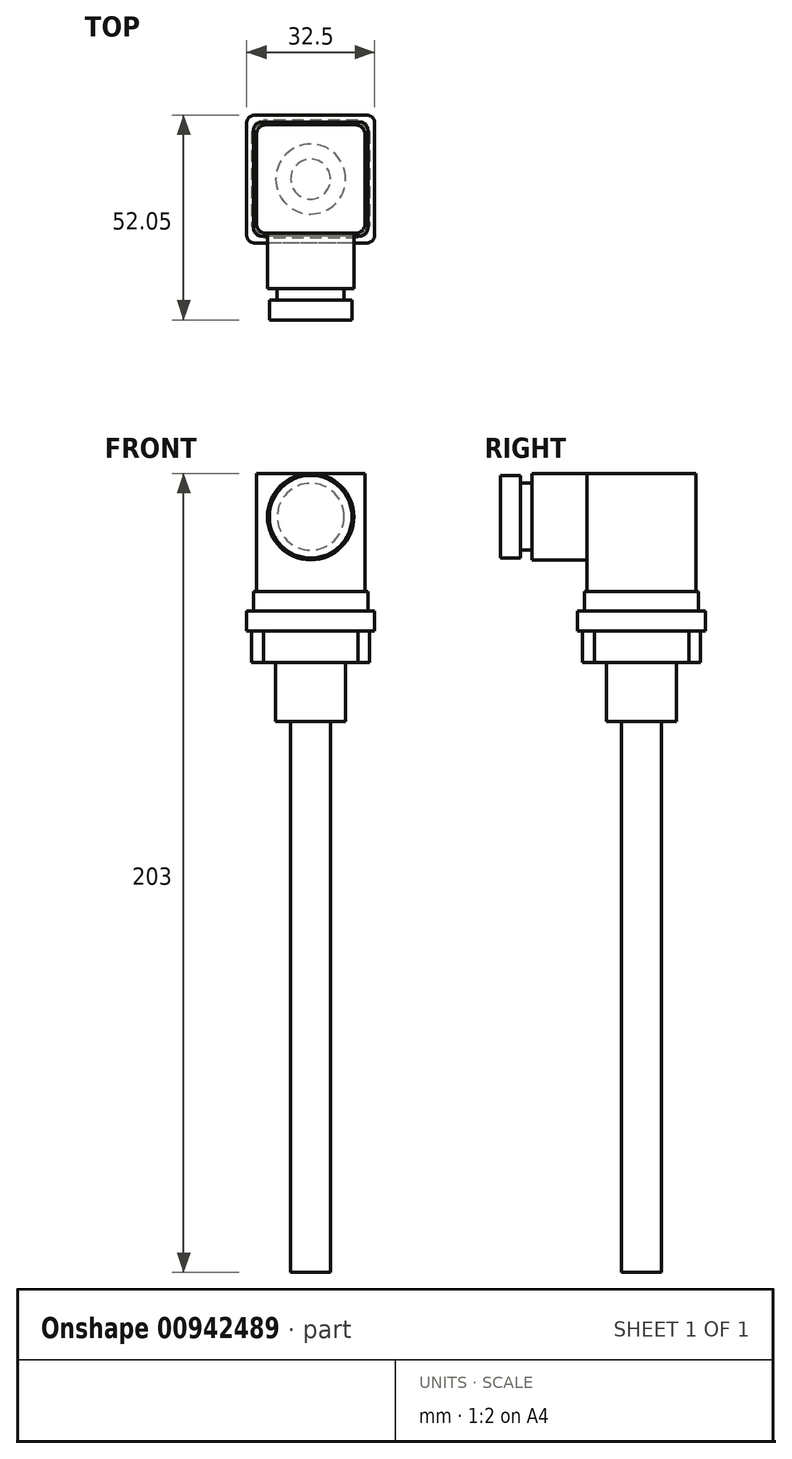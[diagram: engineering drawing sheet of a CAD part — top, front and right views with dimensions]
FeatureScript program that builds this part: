
annotation { "Feature Type Name" : "Feature", "Feature Type Description" : "" }
export const myFeature = defineFeature(function(context is Context, id is Id, definition is map)
    precondition{}
    {
        {
            var Q0;
            Q0=qCreatedBy(makeId("Top.planeOp"),FACE);
            var sketch = newSketch(context, id + "F0", { "sketchPlane" : qUnion([Q0])});
            skLineSegment(sketch, "E0.bottom", {"start": v(13.8, -13.8) * mm, "end": v(-13.8, -13.8) * mm});
            skLineSegment(sketch, "E0.top", {"start": v(13.8, 13.8) * mm, "end": v(-13.8, 13.8) * mm});
            skLineSegment(sketch, "E0.left", {"start": v(13.8, -13.8) * mm, "end": v(13.8, 13.8) * mm});
            skLineSegment(sketch, "E0.right", {"start": v(-13.8, -13.8) * mm, "end": v(-13.8, 13.8) * mm});
            skPoint(sketch, "E0.middle", {"position": v(0, 0) * mm});
            skSolve(sketch);
        }
        {
            var Q0;
            Q0=makeQuery(id+"F0.imprint","IMPRINT",FACE,{"disambiguationData":[TD([[makeQuery(id+"F0.imprint","IMPRINT",EDGE,{"derivedFrom":sQuery(id+"F0.wireOp",EDGE,"E0.bottom")}),-1.0]])]});
            extrude(context, id + "F1", {"entities" : qUnion([Q0]), "depth" : 30 * mm, "offsetDistance" : 25 * mm});
        }
        {
            var Q0;
            Q0=makeQuery(id+"F1.opExtrude","SWEPT_EDGE",EDGE,{"disambiguationData":[OSD([sQuery(id+"F0.wireOp",EDGE,"E0.bottom"),sQuery(id+"F0.wireOp",EDGE,"E0.right")])]});
            var Q1;
            Q1=makeQuery(id+"F1.opExtrude","SWEPT_EDGE",EDGE,{"disambiguationData":[OSD([sQuery(id+"F0.wireOp",EDGE,"E0.bottom"),sQuery(id+"F0.wireOp",EDGE,"E0.left")])]});
            var Q2;
            Q2=makeQuery(id+"F1.opExtrude","SWEPT_EDGE",EDGE,{"disambiguationData":[OSD([sQuery(id+"F0.wireOp",EDGE,"E0.top"),sQuery(id+"F0.wireOp",EDGE,"E0.left")])]});
            var Q3;
            Q3=makeQuery(id+"F1.opExtrude","SWEPT_EDGE",EDGE,{"disambiguationData":[OSD([sQuery(id+"F0.wireOp",EDGE,"E0.top"),sQuery(id+"F0.wireOp",EDGE,"E0.right")])]});
            fillet(context, id + "F2", {"entities" : qUnion([Q0, Q1, Q2, Q3]), "radius" : 2.5 * mm, "tangentPropagation" : true, "allowEdgeOverflow" : false});
        }
        {
            var Q0;
            Q0=makeQuery(id+"F1.opExtrude","SWEPT_FACE",FACE,{"disambiguationData":[OSD([sQuery(id+"F0.wireOp",EDGE,"E0.bottom")])]});
            var sketch = newSketch(context, id + "F3", { "sketchPlane" : qUnion([Q0])});
            skPoint(sketch, "E1", {"position": v(0, 19) * mm});
            skPoint(sketch, "E1.positionSnap0", {"position": v(0, 30) * mm});
            skCircle(sketch, "E2", {"center": v(0, 19) * mm, "radius": 10.97 * mm});
            skSolve(sketch);
        }
        {
            var Q0;
            Q0=makeQuery(id+"F3.imprint","IMPRINT",FACE,{"disambiguationData":[TD([[makeQuery(id+"F3.imprint","IMPRINT",EDGE,{"derivedFrom":sQuery(id+"F3.wireOp",EDGE,"E2")}),1.0]])]});
            extrude(context, id + "F4", {"entities" : qUnion([Q0]), "operationType" : NewBodyOperationType.ADD, "depth" : 14 * mm, "offsetDistance" : 25 * mm});
        }
        {
            var Q0;
            Q0=makeQuery(id+"F4.opExtrude","CAP_FACE",FACE,{"disambiguationData":[OSD([sQuery(id+"F3.wireOp",EDGE,"E2")])],"isStart":false});
            var sketch = newSketch(context, id + "F5", { "sketchPlane" : qUnion([Q0])});
            skPoint(sketch, "E3", {"position": v(0, 19) * mm});
            skCircle(sketch, "E4", {"center": v(0, 19) * mm, "radius": 8.5 * mm});
            skSolve(sketch);
        }
        {
            var Q0;
            Q0=makeQuery(id+"F5.imprint","IMPRINT",FACE,{"disambiguationData":[TD([[makeQuery(id+"F5.imprint","IMPRINT",EDGE,{"derivedFrom":sQuery(id+"F5.wireOp",EDGE,"E4")}),1.0]])]});
            extrude(context, id + "F6", {"entities" : qUnion([Q0]), "operationType" : NewBodyOperationType.ADD, "depth" : 3 * mm, "offsetDistance" : 25 * mm});
        }
        {
            var Q0;
            Q0=makeQuery(id+"F6.opExtrude","CAP_FACE",FACE,{"disambiguationData":[OSD([sQuery(id+"F5.wireOp",EDGE,"E4")])],"isStart":false});
            var sketch = newSketch(context, id + "F7", { "sketchPlane" : qUnion([Q0])});
            skCircle(sketch, "E5", {"center": v(0, 19) * mm, "radius": 10.5 * mm});
            skSolve(sketch);
        }
        {
            var Q0;
            Q0=makeQuery(id+"F7.imprint","IMPRINT",FACE,{"disambiguationData":[TD([[makeQuery(id+"F7.imprint","IMPRINT",EDGE,{"derivedFrom":sQuery(id+"F7.wireOp",EDGE,"E5")}),1.0]])]});
            var Q1;
            Q1=makeQuery(id+"F7.imprint","IMPRINT",FACE,{"disambiguationData":[TD([[makeQuery(id+"F7.imprint","IMPRINT",EDGE,{"derivedFrom":makeQuery(id+"F6.opExtrude","CAP_EDGE",EDGE,{"disambiguationData":[OSD([sQuery(id+"F5.wireOp",EDGE,"E4")])],"isStart":false})}),1.0]])]});
            extrude(context, id + "F8", {"entities" : qUnion([Q0, Q1]), "operationType" : NewBodyOperationType.ADD, "depth" : 5 * mm, "offsetDistance" : 25 * mm});
        }
        {
            var Q0;
            Q0=makeQuery(id+"F1.opExtrude","CAP_FACE",FACE,{"disambiguationData":[OSD([sQuery(id+"F0.wireOp",EDGE,"E0.bottom"),sQuery(id+"F0.wireOp",EDGE,"E0.top"),sQuery(id+"F0.wireOp",EDGE,"E0.left"),sQuery(id+"F0.wireOp",EDGE,"E0.right")])],"isStart":true});
            var sketch = newSketch(context, id + "F9", { "sketchPlane" : qUnion([Q0])});
            skLineSegment(sketch, "E6.bottom", {"start": v(14.5, -14.5) * mm, "end": v(-14.5, -14.5) * mm});
            skLineSegment(sketch, "E6.top", {"start": v(14.5, 14.5) * mm, "end": v(-14.5, 14.5) * mm});
            skLineSegment(sketch, "E6.left", {"start": v(14.5, -14.5) * mm, "end": v(14.5, 14.5) * mm});
            skLineSegment(sketch, "E6.right", {"start": v(-14.5, -14.5) * mm, "end": v(-14.5, 14.5) * mm});
            skPoint(sketch, "E6.middle", {"position": v(0, 0) * mm});
            skSolve(sketch);
        }
        {
            var Q0;
            Q0=makeQuery(id+"F9.imprint","IMPRINT",FACE,{"disambiguationData":[TD([[makeQuery(id+"F9.imprint","IMPRINT",EDGE,{"derivedFrom":sQuery(id+"F9.wireOp",EDGE,"E6.bottom")}),-1.0]])]});
            var Q1;
            {var subQ3=sQuery(id+"F0.wireOp",EDGE,"E0.bottom");Q1=makeQuery(id+"F9.imprint","IMPRINT",FACE,{"disambiguationData":[TD([[makeQuery(id+"F9.imprint","IMPRINT",EDGE,{"derivedFrom":makeQuery(id+"F1.opExtrude","CAP_EDGE",EDGE,{"disambiguationData":[OSD([subQ3])],"isStart":true})}),1.0]])]});}
            extrude(context, id + "F10", {"entities" : qUnion([Q0, Q1]), "operationType" : NewBodyOperationType.ADD, "depth" : 5 * mm, "offsetDistance" : 25 * mm});
        }
        {
            var Q0;
            Q0=makeQuery(id+"F10.opExtrude","SWEPT_EDGE",EDGE,{"disambiguationData":[OSD([sQuery(id+"F9.wireOp",EDGE,"E6.bottom"),sQuery(id+"F9.wireOp",EDGE,"E6.right")])]});
            var Q1;
            Q1=makeQuery(id+"F10.opExtrude","SWEPT_EDGE",EDGE,{"disambiguationData":[OSD([sQuery(id+"F9.wireOp",EDGE,"E6.top"),sQuery(id+"F9.wireOp",EDGE,"E6.right")])]});
            var Q2;
            Q2=makeQuery(id+"F10.opExtrude","SWEPT_EDGE",EDGE,{"disambiguationData":[OSD([sQuery(id+"F9.wireOp",EDGE,"E6.top"),sQuery(id+"F9.wireOp",EDGE,"E6.left")])]});
            var Q3;
            Q3=makeQuery(id+"F10.opExtrude","SWEPT_EDGE",EDGE,{"disambiguationData":[OSD([sQuery(id+"F9.wireOp",EDGE,"E6.bottom"),sQuery(id+"F9.wireOp",EDGE,"E6.left")])]});
            fillet(context, id + "F11", {"entities" : qUnion([Q0, Q1, Q2, Q3]), "radius" : 2 * mm, "tangentPropagation" : true, "allowEdgeOverflow" : false});
        }
        {
            var Q0;
            Q0=makeQuery(id+"F10.opExtrude","CAP_FACE",FACE,{"disambiguationData":[OSD([sQuery(id+"F9.wireOp",EDGE,"E6.bottom"),sQuery(id+"F9.wireOp",EDGE,"E6.top"),sQuery(id+"F9.wireOp",EDGE,"E6.left"),sQuery(id+"F9.wireOp",EDGE,"E6.right")])],"isStart":false});
            var sketch = newSketch(context, id + "F12", { "sketchPlane" : qUnion([Q0])});
            skLineSegment(sketch, "E7.bottom", {"start": v(16.25, -16.25) * mm, "end": v(-16.25, -16.25) * mm});
            skLineSegment(sketch, "E7.top", {"start": v(16.25, 16.25) * mm, "end": v(-16.25, 16.25) * mm});
            skLineSegment(sketch, "E7.left", {"start": v(16.25, -16.25) * mm, "end": v(16.25, 16.25) * mm});
            skLineSegment(sketch, "E7.right", {"start": v(-16.25, -16.25) * mm, "end": v(-16.25, 16.25) * mm});
            skPoint(sketch, "E7.middle", {"position": v(0, 0) * mm});
            skSolve(sketch);
        }
        {
            var Q0;
            Q0=makeQuery(id+"F12.imprint","IMPRINT",FACE,{"disambiguationData":[TD([[makeQuery(id+"F12.imprint","IMPRINT",EDGE,{"derivedFrom":sQuery(id+"F12.wireOp",EDGE,"E7.bottom")}),-1.0]])]});
            var Q1;
            {var subQ3=sQuery(id+"F9.wireOp",EDGE,"E6.bottom");Q1=makeQuery(id+"F12.imprint","IMPRINT",FACE,{"disambiguationData":[TD([[makeQuery(id+"F12.imprint","IMPRINT",EDGE,{"derivedFrom":makeQuery(id+"F10.opExtrude","CAP_EDGE",EDGE,{"disambiguationData":[OSD([subQ3])],"isStart":false})}),-1.0]])]});}
            extrude(context, id + "F13", {"entities" : qUnion([Q0, Q1]), "operationType" : NewBodyOperationType.ADD, "depth" : 5 * mm, "offsetDistance" : 25 * mm});
        }
        {
            var Q0;
            Q0=makeQuery(id+"F13.opExtrude","SWEPT_EDGE",EDGE,{"disambiguationData":[OSD([sQuery(id+"F12.wireOp",EDGE,"E7.top"),sQuery(id+"F12.wireOp",EDGE,"E7.left")])]});
            var Q1;
            Q1=makeQuery(id+"F13.opExtrude","SWEPT_EDGE",EDGE,{"disambiguationData":[OSD([sQuery(id+"F12.wireOp",EDGE,"E7.bottom"),sQuery(id+"F12.wireOp",EDGE,"E7.left")])]});
            var Q2;
            Q2=makeQuery(id+"F13.opExtrude","SWEPT_EDGE",EDGE,{"disambiguationData":[OSD([sQuery(id+"F12.wireOp",EDGE,"E7.bottom"),sQuery(id+"F12.wireOp",EDGE,"E7.right")])]});
            var Q3;
            Q3=makeQuery(id+"F13.opExtrude","SWEPT_EDGE",EDGE,{"disambiguationData":[OSD([sQuery(id+"F12.wireOp",EDGE,"E7.top"),sQuery(id+"F12.wireOp",EDGE,"E7.right")])]});
            fillet(context, id + "F14", {"entities" : qUnion([Q0, Q1, Q2, Q3]), "radius" : 2 * mm, "tangentPropagation" : true, "allowEdgeOverflow" : false});
        }
        {
            var Q0;
            Q0=makeQuery(id+"F13.opExtrude","CAP_FACE",FACE,{"disambiguationData":[OSD([sQuery(id+"F12.wireOp",EDGE,"E7.bottom"),sQuery(id+"F12.wireOp",EDGE,"E7.top"),sQuery(id+"F12.wireOp",EDGE,"E7.left"),sQuery(id+"F12.wireOp",EDGE,"E7.right")])],"isStart":false});
            var sketch = newSketch(context, id + "F15", { "sketchPlane" : qUnion([Q0])});
            skLineSegment(sketch, "E8.bottom", {"start": v(15, -15) * mm, "end": v(-15, -15) * mm});
            skLineSegment(sketch, "E8.top", {"start": v(15, 15) * mm, "end": v(-15, 15) * mm});
            skLineSegment(sketch, "E8.left", {"start": v(15, -15) * mm, "end": v(15, 15) * mm});
            skLineSegment(sketch, "E8.right", {"start": v(-15, -15) * mm, "end": v(-15, 15) * mm});
            skPoint(sketch, "E8.middle", {"position": v(0, 0) * mm});
            skSolve(sketch);
        }
        {
            var Q0;
            Q0=makeQuery(id+"F15.imprint","IMPRINT",FACE,{"disambiguationData":[TD([[makeQuery(id+"F15.imprint","IMPRINT",EDGE,{"derivedFrom":sQuery(id+"F15.wireOp",EDGE,"E8.bottom")}),-1.0]])]});
            extrude(context, id + "F16", {"entities" : qUnion([Q0]), "operationType" : NewBodyOperationType.ADD, "depth" : 8 * mm, "offsetDistance" : 25 * mm});
        }
        {
            var Q0;
            Q0=makeQuery(id+"F16.opExtrude","SWEPT_EDGE",EDGE,{"disambiguationData":[OSD([sQuery(id+"F15.wireOp",EDGE,"E8.top"),sQuery(id+"F15.wireOp",EDGE,"E8.right")])]});
            var Q1;
            Q1=makeQuery(id+"F16.opExtrude","SWEPT_EDGE",EDGE,{"disambiguationData":[OSD([sQuery(id+"F15.wireOp",EDGE,"E8.top"),sQuery(id+"F15.wireOp",EDGE,"E8.left")])]});
            var Q2;
            Q2=makeQuery(id+"F16.opExtrude","SWEPT_EDGE",EDGE,{"disambiguationData":[OSD([sQuery(id+"F15.wireOp",EDGE,"E8.bottom"),sQuery(id+"F15.wireOp",EDGE,"E8.left")])]});
            var Q3;
            Q3=makeQuery(id+"F16.opExtrude","SWEPT_EDGE",EDGE,{"disambiguationData":[OSD([sQuery(id+"F15.wireOp",EDGE,"E8.bottom"),sQuery(id+"F15.wireOp",EDGE,"E8.right")])]});
            chamfer(context, id + "F17", {"entities" : qUnion([Q0, Q1, Q2, Q3]), "width" : 3 * mm, "tangentPropagation" : true});
        }
        {
            var Q0;
            Q0=makeQuery(id+"F16.opExtrude","CAP_FACE",FACE,{"disambiguationData":[OSD([sQuery(id+"F15.wireOp",EDGE,"E8.bottom"),sQuery(id+"F15.wireOp",EDGE,"E8.top"),sQuery(id+"F15.wireOp",EDGE,"E8.left"),sQuery(id+"F15.wireOp",EDGE,"E8.right")])],"isStart":false});
            var sketch = newSketch(context, id + "F18", { "sketchPlane" : qUnion([Q0])});
            skCircle(sketch, "E9", {"center": v(0, 0) * mm, "radius": 8.88 * mm});
            skSolve(sketch);
        }
        {
            var Q0;
            Q0=makeQuery(id+"F18.imprint","IMPRINT",FACE,{"disambiguationData":[TD([[makeQuery(id+"F18.imprint","IMPRINT",EDGE,{"derivedFrom":sQuery(id+"F18.wireOp",EDGE,"E9")}),1.0]])]});
            extrude(context, id + "F19", {"entities" : qUnion([Q0]), "operationType" : NewBodyOperationType.ADD, "depth" : 15 * mm, "offsetDistance" : 25 * mm});
        }
        {
            var Q0;
            Q0=makeQuery(id+"F19.opExtrude","CAP_FACE",FACE,{"disambiguationData":[OSD([sQuery(id+"F18.wireOp",EDGE,"E9")])],"isStart":false});
            var sketch = newSketch(context, id + "F20", { "sketchPlane" : qUnion([Q0])});
            skCircle(sketch, "E10", {"center": v(0, 0) * mm, "radius": 5.07 * mm});
            skSolve(sketch);
        }
        {
            var Q0;
            Q0=makeQuery(id+"F20.imprint","IMPRINT",FACE,{"disambiguationData":[TD([[makeQuery(id+"F20.imprint","IMPRINT",EDGE,{"derivedFrom":sQuery(id+"F20.wireOp",EDGE,"E10")}),1.0]])]});
            extrude(context, id + "F21", {"entities" : qUnion([Q0]), "operationType" : NewBodyOperationType.ADD, "depth" : 140 * mm, "offsetDistance" : 25 * mm});
        }
    });
